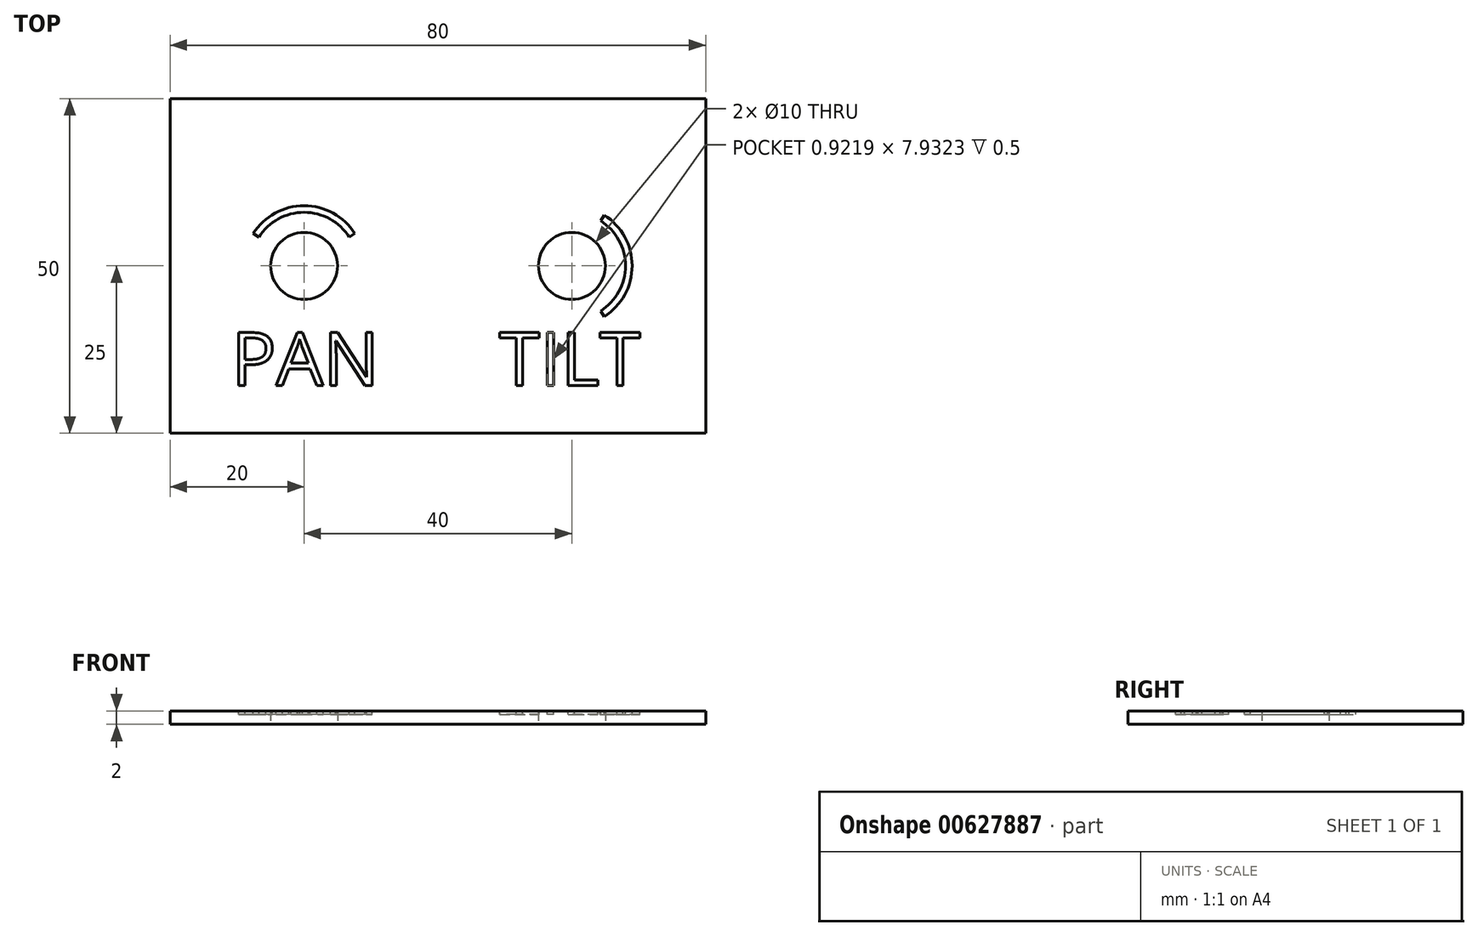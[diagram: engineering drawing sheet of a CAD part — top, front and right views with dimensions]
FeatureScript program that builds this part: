
annotation { "Feature Type Name" : "Feature", "Feature Type Description" : "" }
export const myFeature = defineFeature(function(context is Context, id is Id, definition is map)
    precondition{}
    {
        {
            var Q0;
            Q0=qCreatedBy(makeId("Top.planeOp"),FACE);
            var sketch = newSketch(context, id + "F0", { "sketchPlane" : qUnion([Q0])});
            skLineSegment(sketch, "E0", {"start": v(0, 0) * mm, "end": v(0, 25) * mm, "construction": true});
            skLineSegment(sketch, "E1", {"start": v(0, 0) * mm, "end": v(40, 0) * mm, "construction": true});
            skCircle(sketch, "E2", {"center": v(20, 0) * mm, "radius": 5 * mm});
            skCircle(sketch, "E3.MirrorC", {"center": v(-20, 0) * mm, "radius": 5 * mm});
            skLineSegment(sketch, "E4.bottom", {"start": v(-40, 25) * mm, "end": v(40, 25) * mm});
            skLineSegment(sketch, "E4.top", {"start": v(-40, -25) * mm, "end": v(40, -25) * mm});
            skLineSegment(sketch, "E4.left", {"start": v(-40, 25) * mm, "end": v(-40, -25) * mm});
            skLineSegment(sketch, "E4.right", {"start": v(40, 25) * mm, "end": v(40, -25) * mm});
            skSolve(sketch);
        }
        {
            var Q0;
            Q0 = qSketchRegion(id + "F0", true);
            extrude(context, id + "F1", {"entities" : qUnion([Q0]), "depth" : 2 * mm, "offsetDistance" : 25 * mm});
        }
        {
            var Q0;
            Q0=makeQuery(id+"F1.opExtrude","CAP_FACE",FACE,{"disambiguationData":[OSD([sQuery(id+"F0.wireOp",EDGE,"E2"),sQuery(id+"F0.wireOp",EDGE,"E3.MirrorC"),sQuery(id+"F0.wireOp",EDGE,"E4.bottom"),sQuery(id+"F0.wireOp",EDGE,"E4.top"),sQuery(id+"F0.wireOp",EDGE,"E4.left"),sQuery(id+"F0.wireOp",EDGE,"E4.right")])],"isStart":false});
            var sketch = newSketch(context, id + "F2", { "sketchPlane" : qUnion([Q0])});
            skText(sketch, "E5", { "text": "PAN", "fontName": "OpenSans-Regular.ttf"});
            skText(sketch, "E6", { "text": "TILT", "fontName": "OpenSans-Regular.ttf"});
            skLineSegment(sketch, "E7", {"start": v(-20, 0) * mm, "end": v(-20, -23.24) * mm, "construction": true});
            skLineSegment(sketch, "E8", {"start": v(20, 0) * mm, "end": v(20, -27.12) * mm, "construction": true});
            const initialGuessF2  = {"E5": [-0.03086, -0.0179, 1, 0, 0.008], "E6": [0.00911, -0.0179, 1, 0, 0.008]};
            skSetInitialGuess(sketch, initialGuessF2);
            skSolve(sketch);
        }
        {
            var Q0;
            Q0 = qSketchRegion(id + "F2", true);
            extrude(context, id + "F3", {"entities" : qUnion([Q0]), "operationType" : NewBodyOperationType.REMOVE, "oppositeDirection" : true, "depth" : .5 * mm, "offsetDistance" : 25 * mm});
        }
        {
            var Q0;
            {var subQ0=sQuery(id+"F0.wireOp",EDGE,"E4.bottom");var subQ1=sQuery(id+"F0.wireOp",EDGE,"E4.right");var subQ2=sQuery(id+"F0.wireOp",EDGE,"E4.left");var subQ3=sQuery(id+"F0.wireOp",EDGE,"E2");var subQ4=sQuery(id+"F0.wireOp",EDGE,"E4.top");var subQ5=sQuery(id+"F0.wireOp",EDGE,"E3.MirrorC");Q0=makeQuery(id+"F3.boolean.opBoolean","SPLIT",FACE,{"disambiguationData":[TD([makeQuery(id+"F1.opExtrude","SWEPT_FACE",FACE,{"disambiguationData":[OSD([subQ3])]})])],"derivedFrom":makeQuery(id+"F1.opExtrude","CAP_FACE",FACE,{"disambiguationData":[OSD([subQ3,subQ5,subQ0,subQ4,subQ2,subQ1])],"isStart":false})});}
            var sketch = newSketch(context, id + "F4", { "sketchPlane" : qUnion([Q0])});
            skArc(sketch, "E9", {"start": v(-13.25, 4.3) * mm, "mid": v(-20, 8) * mm, "end": v(-26.75, 4.3) * mm});
            skArc(sketch, "E10.0", {"start": v(-12.4, 4.84) * mm, "mid": v(-20, 9) * mm, "end": v(-27.6, 4.84) * mm});
            skLineSegment(sketch, "E11", {"start": v(-20, 0) * mm, "end": v(-20, 12.3) * mm, "construction": true});
            skLineSegment(sketch, "E12", {"start": v(-20, 0) * mm, "end": v(-10.52, 6.04) * mm, "construction": true});
            skLineSegment(sketch, "E13.MirrorCS", {"start": v(-20, 0) * mm, "end": v(-29.48, 6.04) * mm, "construction": true});
            skLineSegment(sketch, "E14", {"start": v(-27.6, 4.84) * mm, "end": v(-26.75, 4.3) * mm});
            skLineSegment(sketch, "E15", {"start": v(-13.25, 4.3) * mm, "end": v(-12.4, 4.84) * mm});
            skArc(sketch, "E16", {"start": v(24.3, -6.75) * mm, "mid": v(28, 0) * mm, "end": v(24.3, 6.75) * mm});
            skArc(sketch, "E17.0", {"start": v(24.84, -7.6) * mm, "mid": v(29, 0) * mm, "end": v(24.84, 7.6) * mm});
            skLineSegment(sketch, "E18", {"start": v(20, 0) * mm, "end": v(33.85, 0) * mm, "construction": true});
            skLineSegment(sketch, "E19", {"start": v(20, 0) * mm, "end": v(25.63, 8.84) * mm, "construction": true});
            skLineSegment(sketch, "E20.MirrorCS", {"start": v(20, 0) * mm, "end": v(25.63, -8.84) * mm, "construction": true});
            skLineSegment(sketch, "E21", {"start": v(24.3, 6.75) * mm, "end": v(24.84, 7.6) * mm});
            skLineSegment(sketch, "E22", {"start": v(24.3, -6.75) * mm, "end": v(24.84, -7.6) * mm});
            skSolve(sketch);
        }
        {
            var Q0;
            Q0 = qSketchRegion(id + "F4", true);
            extrude(context, id + "F5", {"entities" : qUnion([Q0]), "operationType" : NewBodyOperationType.REMOVE, "oppositeDirection" : true, "depth" : .5 * mm, "offsetDistance" : 25 * mm});
        }
    });
